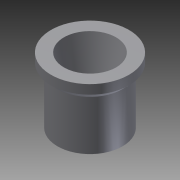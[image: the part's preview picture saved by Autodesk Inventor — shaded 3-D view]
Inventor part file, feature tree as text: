
AUTODESK INVENTOR PART (.ipt)
format: ipt  version: 2012 (Build 160160000, 160)  size: 109,056 bytes
history: native  units: mm
features: extrude x3, sketch x3, chamfer x2
ambient origin geometry x8: Origin, YZ Plane, XZ Plane, XY Plane, X Axis, Y Axis, Z Axis, Center Point
bodies: Solid1 (feature_tree)
feature tree (8):
  extrude  "Extrusion1"  Depth=8.0mm
  extrude  "Extrusion2"  Depth=23.9mm
  chamfer  "Chamfer1"  Distance=4.8mm
  extrude  "Extrusion3"  Depth=10.0mm
  chamfer  "Chamfer2"  Distance=18.0mm
  sketch  "Sketch1"  dims[d0=19.9mm d1=8.0mm]
  sketch  "Sketch2"  dims[d2=20.0mm d3=0.0mm d4=23.9mm d5=4.8mm d6=0.0mm]
  sketch  "Sketch3"  dims[d7=2.0mm d8=2.0mm d9=45.0deg d10=10.0mm d11=18.0mm d12=0.0mm d13=3.0mm d14=13.5mm d15=45.0deg]
